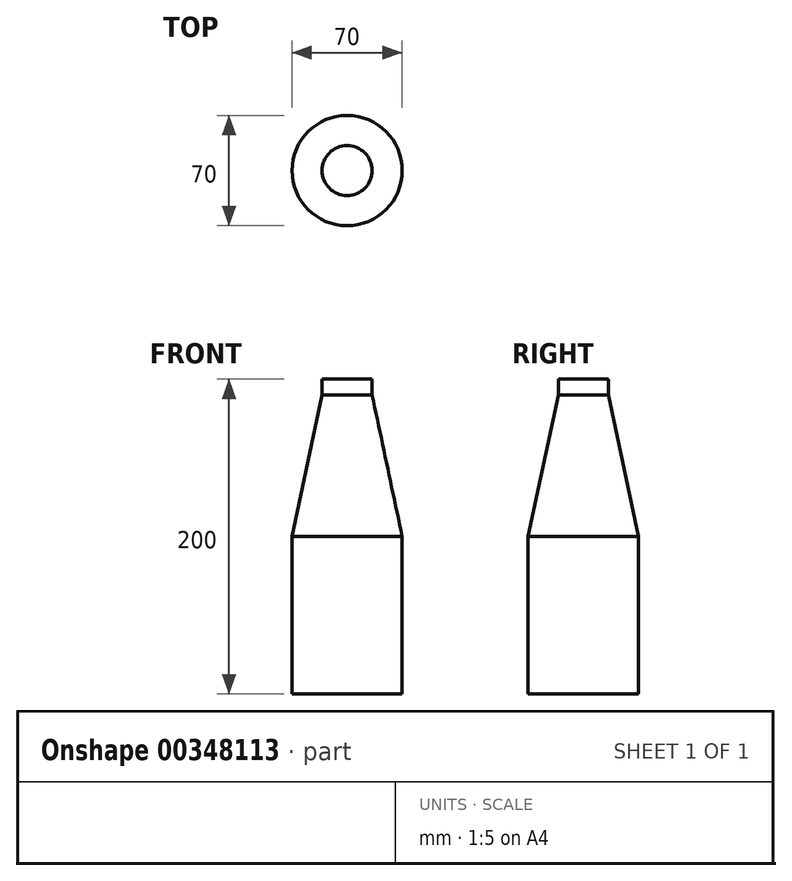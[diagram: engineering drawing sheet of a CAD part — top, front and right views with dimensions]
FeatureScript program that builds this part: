
annotation { "Feature Type Name" : "Feature", "Feature Type Description" : "" }
export const myFeature = defineFeature(function(context is Context, id is Id, definition is map)
    precondition{}
    {
        {
            var Q0;
            Q0=qCreatedBy(makeId("Top.planeOp"),FACE);
            var sketch = newSketch(context, id + "F0", { "sketchPlane" : qUnion([Q0])});
            skCircle(sketch, "E0", {"center": v(0, 0) * mm, "radius": 35 * mm});
            skSolve(sketch);
        }
        {
            var Q0;
            Q0=makeQuery(id+"F0.imprint","IMPRINT",FACE,{"disambiguationData":[TD([[makeQuery(id+"F0.imprint","IMPRINT",EDGE,{"derivedFrom":sQuery(id+"F0.wireOp",EDGE,"E0")}),1.0]])]});
            extrude(context, id + "F1", {"entities" : qUnion([Q0]), "depth" : 100 * mm});
        }
        {
            var Q0;
            Q0=makeQuery(id+"F1.opExtrude","CAP_FACE",FACE,{"disambiguationData":[OSD([sQuery(id+"F0.wireOp",EDGE,"E0")])],"isStart":false});
            extrude(context, id + "F2", {"entities" : qUnion([Q0]), "operationType" : NewBodyOperationType.ADD, "depth" : 90 * mm, "hasDraft" : true, "draftAngle" : 12 * degree, "draftPullDirection" : true});
        }
        {
            var Q0;
            Q0=makeQuery(id+"F2.opExtrude","CAP_FACE",FACE,{"disambiguationData":[OSD([sQuery(id+"F0.wireOp",EDGE,"E0")])],"isStart":false});
            extrude(context, id + "F3", {"entities" : qUnion([Q0]), "operationType" : NewBodyOperationType.ADD, "depth" : 10 * mm});
        }
    });
